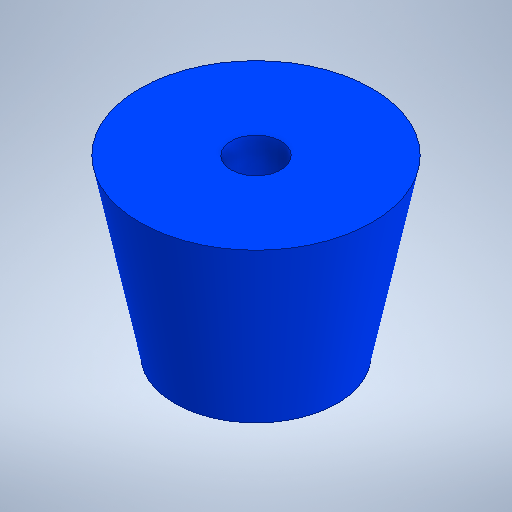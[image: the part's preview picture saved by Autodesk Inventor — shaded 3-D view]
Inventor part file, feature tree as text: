
AUTODESK INVENTOR PART (.ipt)
format: ipt  version: 2025.2 (Build 292293000, 293)  size: 223,232 bytes
history: native  units: mm
features: revolve x1, sketch x1
ambient origin geometry x8: Origin, YZ Plane, XZ Plane, XY Plane, X Axis, Y Axis, Z Axis, Center Point
bodies: Solid1 (feature_tree)
feature tree (2):
  revolve  "Revolution1"  [1 undecoded]
  sketch  "Sketch1"  dims[d0=7.0mm d1=15.0mm d2=3.0mm d3=2.15mm d4=11.0mm d5=4.0mm d6=90.0deg]
note: 1 required parameter value undecoded (feature->parameter linkage not recoverable at this tier; creation-order binding heuristic only, values carry confidence <= 0.55)
